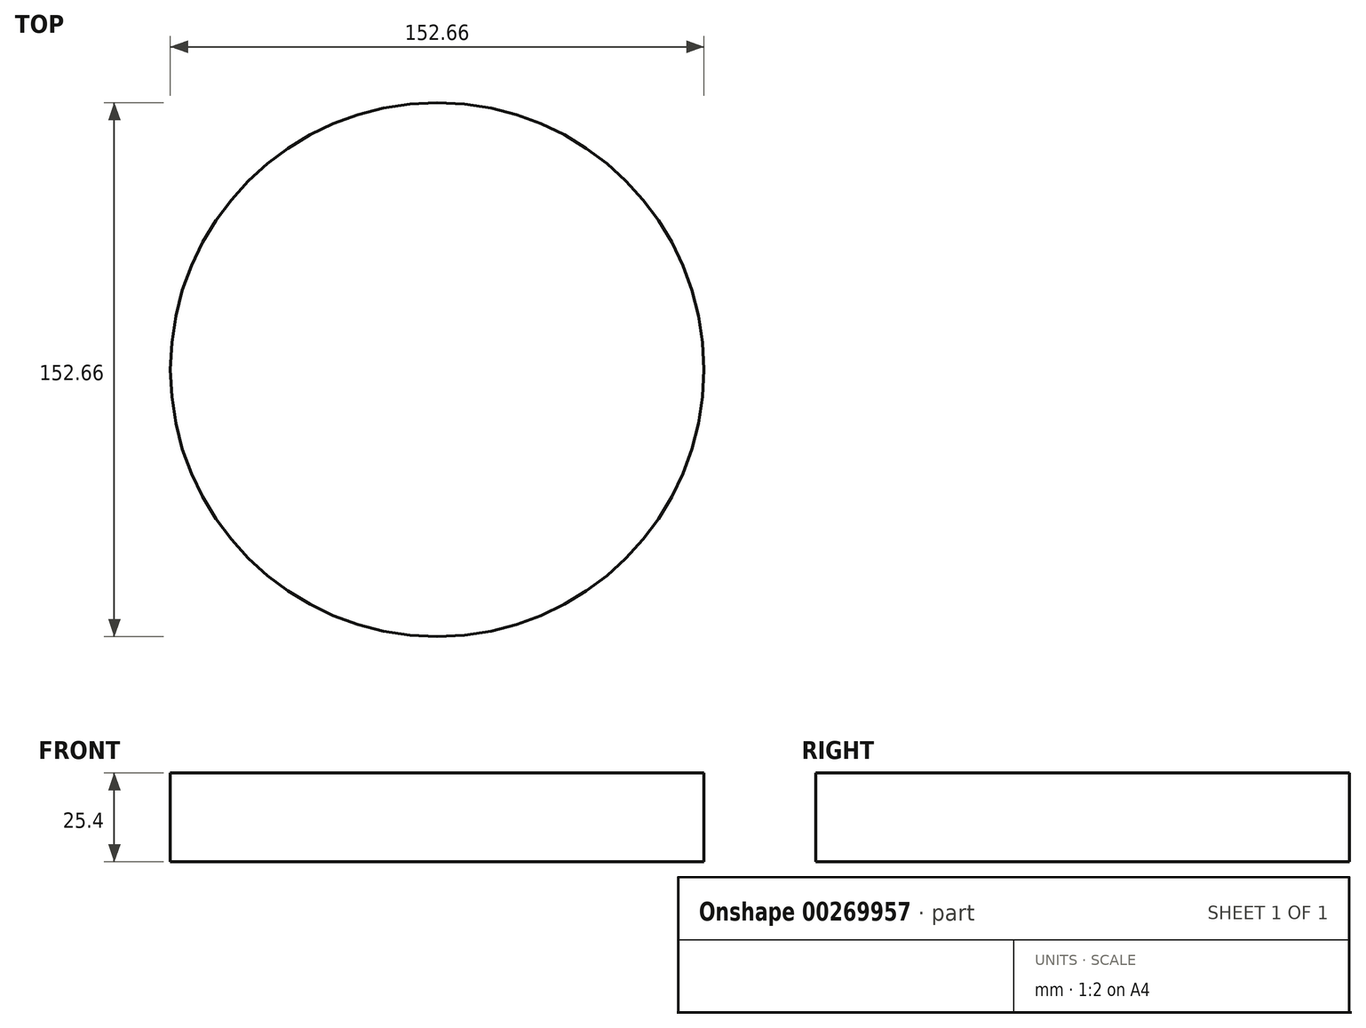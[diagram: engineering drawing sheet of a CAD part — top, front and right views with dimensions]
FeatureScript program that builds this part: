
annotation { "Feature Type Name" : "Feature", "Feature Type Description" : "" }
export const myFeature = defineFeature(function(context is Context, id is Id, definition is map)
    precondition{}
    {
        {
            var Q0;
            Q0=qCreatedBy(makeId("Top.planeOp"),FACE);
            var sketch = newSketch(context, id + "F0", { "sketchPlane" : qUnion([Q0])});
            skCircle(sketch, "E0", {"center": v(0, 0) * mm, "radius": 76.33 * mm});
            skSolve(sketch);
        }
        {
            var Q0;
            Q0 = qSketchRegion(id + "F0", true);
            extrude(context, id + "F1", {"entities" : qUnion([Q0]), "depth" : 25.4 * mm});
        }
    });
